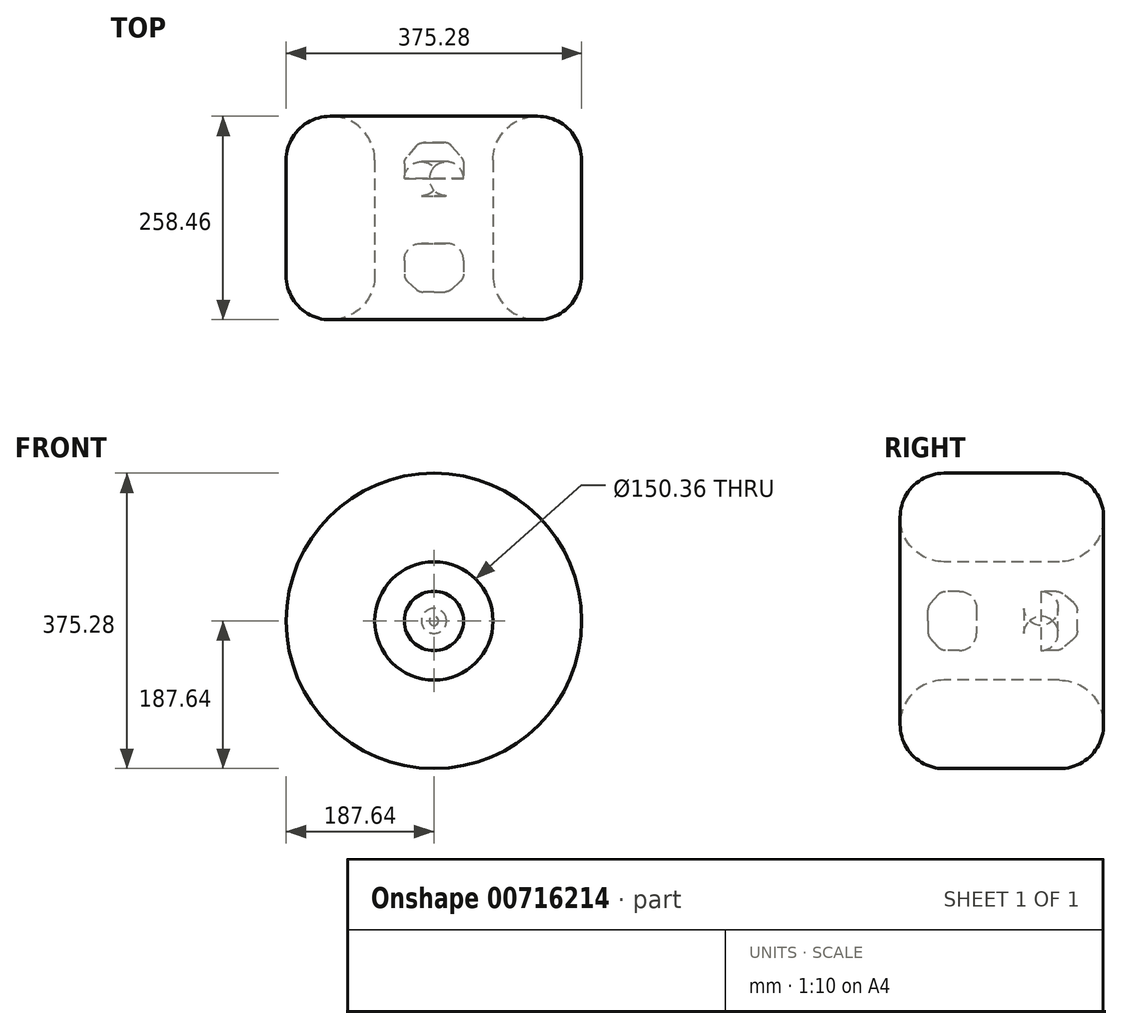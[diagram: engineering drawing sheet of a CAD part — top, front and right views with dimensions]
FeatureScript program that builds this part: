
annotation { "Feature Type Name" : "Feature", "Feature Type Description" : "" }
export const myFeature = defineFeature(function(context is Context, id is Id, definition is map)
    precondition{}
    {
        {
            var Q0;
            Q0=qCreatedBy(makeId("Right.planeOp"),FACE);
            var sketch = newSketch(context, id + "F0", { "sketchPlane" : qUnion([Q0])});
            skLineSegment(sketch, "E0.bottom", {"start": v(-128.2, 187.64) * mm, "end": v(130.26, 187.64) * mm});
            skLineSegment(sketch, "E0.top", {"start": v(-128.2, 75.18) * mm, "end": v(130.26, 75.18) * mm});
            skLineSegment(sketch, "E0.left", {"start": v(-128.2, 187.64) * mm, "end": v(-128.2, 75.18) * mm});
            skLineSegment(sketch, "E0.right", {"start": v(130.26, 187.64) * mm, "end": v(130.26, 75.18) * mm});
            skLineSegment(sketch, "E1.bottom", {"start": v(-31.12, 75.18) * mm, "end": v(29.2, 75.18) * mm});
            skLineSegment(sketch, "E1.top", {"start": v(-31.12, 0) * mm, "end": v(29.2, 0) * mm});
            skLineSegment(sketch, "E1.left", {"start": v(-31.12, 75.18) * mm, "end": v(-31.12, 0) * mm});
            skLineSegment(sketch, "E1.right", {"start": v(29.2, 75.18) * mm, "end": v(29.2, 0) * mm});
            skLineSegment(sketch, "E2.bottom", {"start": v(-31.12, 37.6) * mm, "end": v(-76.03, 37.6) * mm});
            skLineSegment(sketch, "E2.top", {"start": v(-31.12, 0) * mm, "end": v(-76.03, 0) * mm});
            skLineSegment(sketch, "E2.left", {"start": v(-31.12, 37.6) * mm, "end": v(-31.12, 0) * mm});
            skLineSegment(sketch, "E2.right", {"start": v(-76.03, 37.6) * mm, "end": v(-76.03, 0) * mm});
            skLineSegment(sketch, "E3.bottom", {"start": v(29.2, 37.6) * mm, "end": v(74.84, 37.6) * mm});
            skLineSegment(sketch, "E3.top", {"start": v(29.2, 0) * mm, "end": v(74.84, 0) * mm});
            skLineSegment(sketch, "E3.left", {"start": v(29.2, 37.6) * mm, "end": v(29.2, 0) * mm});
            skLineSegment(sketch, "E3.right", {"start": v(74.84, 37.6) * mm, "end": v(74.84, 0) * mm});
            skLineSegment(sketch, "E4", {"start": v(-76.03, 37.6) * mm, "end": v(-92.82, 18.8) * mm});
            skPoint(sketch, "E4.endSnap0", {"position": v(-76.03, 18.8) * mm});
            skLineSegment(sketch, "E5", {"start": v(-92.82, 18.8) * mm, "end": v(-92.97, 0) * mm});
            skLineSegment(sketch, "E6", {"start": v(-92.97, 0) * mm, "end": v(-76.03, 0) * mm});
            skLineSegment(sketch, "E7", {"start": v(74.84, 0) * mm, "end": v(96.82, 0) * mm});
            skLineSegment(sketch, "E8", {"start": v(96.82, 0) * mm, "end": v(96.82, 18.8) * mm});
            skPoint(sketch, "E8.endSnap0", {"position": v(74.84, 18.8) * mm});
            skLineSegment(sketch, "E9", {"start": v(96.82, 18.8) * mm, "end": v(74.84, 37.6) * mm});
            skSolve(sketch);
        }
        {
            var Q0;
            Q0=makeQuery(id+"F0.imprint","IMPRINT",FACE,{"disambiguationData":[TD([[makeQuery(id+"F0.imprint","IMPRINT",EDGE,{"derivedFrom":sQuery(id+"F0.wireOp",EDGE,"E0.bottom")}),-1.0]])]});
            var sketch = newSketch(context, id + "F1", { "sketchPlane" : qUnion([Q0])});
            skSolve(sketch);
        }
        {
            var Q0;
            Q0=makeQuery(id+"F1.imprint","IMPRINT",FACE,{"disambiguationData":[TD([[makeQuery(id+"F1.imprint","IMPRINT",EDGE,{"derivedFrom":makeQuery(id+"F0.imprint","IMPRINT",EDGE,{"derivedFrom":sQuery(id+"F0.wireOp",EDGE,"E0.bottom")})}),-1.0]])]});
            var Q1;
            Q1=sQuery(id+"F0.wireOp",EDGE,"E1.top");
            revolve(context, id + "F2", {"surfaceOperationType" : NewSurfaceOperationType.NEW, "entities" : qUnion([Q0]), "axis" : qUnion([Q1]), "revolveType" : RevolveType.FULL});
        }
        {
            var Q0;
            Q0=makeQuery(id+"F0.imprint","IMPRINT",FACE,{"disambiguationData":[TD([[makeQuery(id+"F0.imprint","IMPRINT",EDGE,{"derivedFrom":sQuery(id+"F0.wireOp",EDGE,"E1.bottom")}),-1.0]])]});
            var Q1;
            Q1=makeQuery(id+"F0.imprint","IMPRINT",FACE,{"disambiguationData":[TD([[makeQuery(id+"F0.imprint","IMPRINT",EDGE,{"derivedFrom":sQuery(id+"F0.wireOp",EDGE,"E2.bottom")}),1.0]])]});
            var Q2;
            Q2=makeQuery(id+"F0.imprint","IMPRINT",FACE,{"disambiguationData":[TD([[makeQuery(id+"F0.imprint","IMPRINT",EDGE,{"derivedFrom":sQuery(id+"F0.wireOp",EDGE,"E2.right")}),-1.0]])]});
            var Q3;
            Q3=makeQuery(id+"F0.imprint","IMPRINT",FACE,{"disambiguationData":[TD([[makeQuery(id+"F0.imprint","IMPRINT",EDGE,{"derivedFrom":sQuery(id+"F0.wireOp",EDGE,"E3.bottom")}),-1.0]])]});
            var Q4;
            Q4=makeQuery(id+"F0.imprint","IMPRINT",FACE,{"disambiguationData":[TD([[makeQuery(id+"F0.imprint","IMPRINT",EDGE,{"derivedFrom":sQuery(id+"F0.wireOp",EDGE,"E3.right")}),1.0]])]});
            var Q5;
            Q5=sQuery(id+"F0.wireOp",EDGE,"E1.top");
            revolve(context, id + "F3", {"surfaceOperationType" : NewSurfaceOperationType.NEW, "entities" : qUnion([Q0, Q1, Q2, Q3, Q4]), "axis" : qUnion([Q5]), "revolveType" : RevolveType.FULL});
        }
        {
            var Q0;
            Q0=makeQuery(id+"F2.opRevolve","SWEPT_EDGE",EDGE,{"disambiguationData":[OSD([sQuery(id+"F0.wireOp",EDGE,"E0.bottom"),sQuery(id+"F0.wireOp",EDGE,"E0.left")])]});
            var Q1;
            Q1=makeQuery(id+"F2.opRevolve","SWEPT_EDGE",EDGE,{"disambiguationData":[OSD([sQuery(id+"F0.wireOp",EDGE,"E0.bottom"),sQuery(id+"F0.wireOp",EDGE,"E0.right")])]});
            var Q2;
            Q2=makeQuery(id+"F2.opRevolve","SWEPT_EDGE",EDGE,{"disambiguationData":[OSD([sQuery(id+"F0.wireOp",EDGE,"E0.top"),sQuery(id+"F0.wireOp",EDGE,"E0.right")])]});
            var Q3;
            Q3=makeQuery(id+"F2.opRevolve","SWEPT_EDGE",EDGE,{"disambiguationData":[OSD([sQuery(id+"F0.wireOp",EDGE,"E0.top"),sQuery(id+"F0.wireOp",EDGE,"E0.left")])]});
            fillet(context, id + "F4", {"entities" : qUnion([Q0, Q1, Q2, Q3]), "radius" : 55.9 * mm, "tangentPropagation" : true, "allowEdgeOverflow" : false});
        }
        {
            var Q0;
            Q0=makeQuery(id+"F3.opRevolve","SWEPT_EDGE",EDGE,{"disambiguationData":[OSD([sQuery(id+"F0.wireOp",EDGE,"E2.bottom"),sQuery(id+"F0.wireOp",EDGE,"E2.right"),sQuery(id+"F0.wireOp",EDGE,"E4")])]});
            var Q1;
            Q1=makeQuery(id+"F3.opRevolve","SWEPT_EDGE",EDGE,{"disambiguationData":[OSD([sQuery(id+"F0.wireOp",EDGE,"E4"),sQuery(id+"F0.wireOp",EDGE,"E5")])]});
            var Q2;
            Q2=makeQuery(id+"F3.opRevolve","SWEPT_EDGE",EDGE,{"disambiguationData":[OSD([sQuery(id+"F0.wireOp",EDGE,"E3.bottom"),sQuery(id+"F0.wireOp",EDGE,"E3.right"),sQuery(id+"F0.wireOp",EDGE,"E9")])]});
            var Q3;
            Q3=makeQuery(id+"F3.opRevolve","SWEPT_EDGE",EDGE,{"disambiguationData":[OSD([sQuery(id+"F0.wireOp",EDGE,"E8"),sQuery(id+"F0.wireOp",EDGE,"E9")])]});
            fillet(context, id + "F5", {"entities" : qUnion([Q0, Q1, Q2, Q3]), "radius" : 12.55 * mm, "tangentPropagation" : true, "allowEdgeOverflow" : false});
        }
        {
            var Q0;
            Q0=makeQuery(id+"F3.opRevolve","SWEPT_EDGE",EDGE,{"disambiguationData":[OSD([sQuery(id+"F0.wireOp",EDGE,"E1.left"),sQuery(id+"F0.wireOp",EDGE,"E2.bottom"),sQuery(id+"F0.wireOp",EDGE,"E2.left")])]});
            var Q1;
            Q1=makeQuery(id+"F3.opRevolve","SWEPT_EDGE",EDGE,{"disambiguationData":[OSD([sQuery(id+"F0.wireOp",EDGE,"E1.right"),sQuery(id+"F0.wireOp",EDGE,"E3.bottom"),sQuery(id+"F0.wireOp",EDGE,"E3.left")])]});
            fillet(context, id + "F6", {"entities" : qUnion([Q0, Q1]), "radius" : 21.67 * mm, "tangentPropagation" : true, "allowEdgeOverflow" : false});
        }
    });
